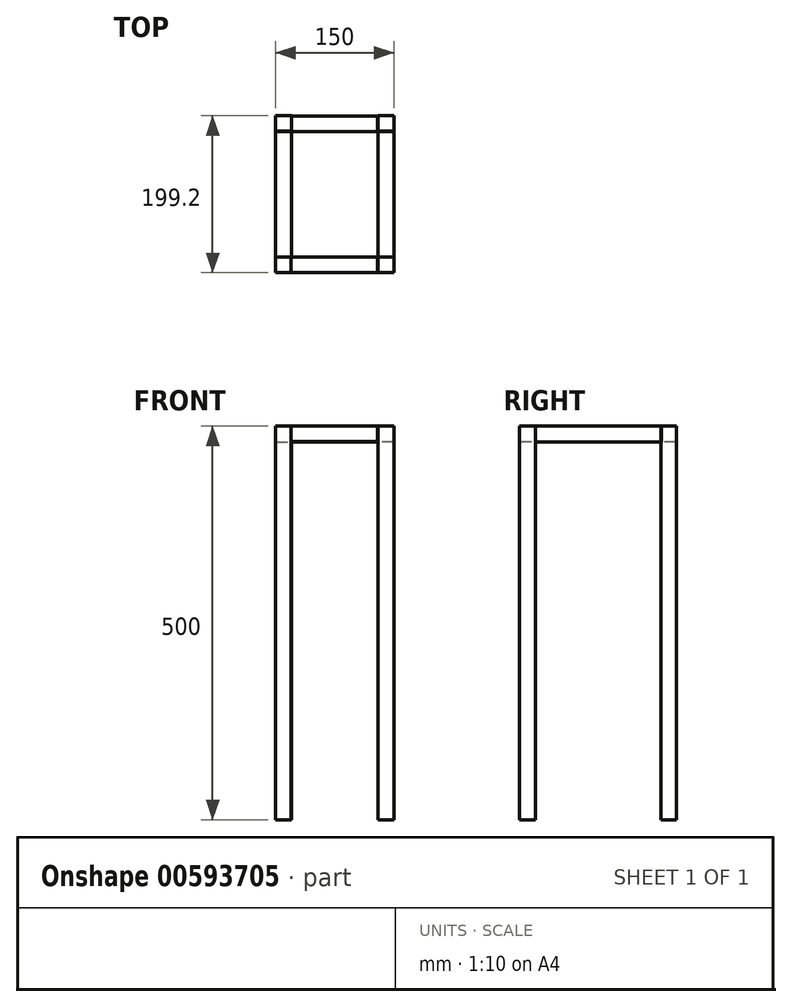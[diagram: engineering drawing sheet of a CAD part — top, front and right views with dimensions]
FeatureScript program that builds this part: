
annotation { "Feature Type Name" : "Feature", "Feature Type Description" : "" }
export const myFeature = defineFeature(function(context is Context, id is Id, definition is map)
    precondition{}
    {
        {
            var Q0;
            Q0=qCreatedBy(makeId("Top.planeOp"),FACE);
            var sketch = newSketch(context, id + "F0", { "sketchPlane" : qUnion([Q0])});
            skLineSegment(sketch, "E0.bottom", {"start": v(0, 0) * mm, "end": v(19.4, 0) * mm});
            skLineSegment(sketch, "E0.top", {"start": v(0, 20) * mm, "end": v(19.4, 20) * mm});
            skLineSegment(sketch, "E0.left", {"start": v(0, 0) * mm, "end": v(0, 20) * mm});
            skLineSegment(sketch, "E0.right", {"start": v(19.4, 0) * mm, "end": v(19.4, 20) * mm});
            skSolve(sketch);
        }
        {
            var Q0;
            Q0=qCreatedBy(makeId("Top.planeOp"),FACE);
            var sketch = newSketch(context, id + "F1", { "sketchPlane" : qUnion([Q0])});
            skLineSegment(sketch, "E1.bottom", {"start": v(0, 0) * mm, "end": v(150, 0) * mm, "construction": true});
            skLineSegment(sketch, "E1.top", {"start": v(0, 199.2) * mm, "end": v(150, 199.2) * mm, "construction": true});
            skLineSegment(sketch, "E1.left", {"start": v(0, 0) * mm, "end": v(0, 199.2) * mm, "construction": true});
            skLineSegment(sketch, "E1.right", {"start": v(150, 0) * mm, "end": v(150, 199.2) * mm, "construction": true});
            skLineSegment(sketch, "E2.bottom", {"start": v(0, 199.2) * mm, "end": v(20, 199.2) * mm});
            skLineSegment(sketch, "E2.top", {"start": v(0, 179.2) * mm, "end": v(20, 179.2) * mm});
            skLineSegment(sketch, "E2.left", {"start": v(0, 199.2) * mm, "end": v(0, 179.2) * mm});
            skLineSegment(sketch, "E2.right", {"start": v(20, 199.2) * mm, "end": v(20, 179.2) * mm});
            skLineSegment(sketch, "E3.bottom", {"start": v(150, 199.2) * mm, "end": v(130, 199.2) * mm});
            skLineSegment(sketch, "E3.top", {"start": v(150, 179.2) * mm, "end": v(130, 179.2) * mm});
            skLineSegment(sketch, "E3.left", {"start": v(150, 199.2) * mm, "end": v(150, 179.2) * mm});
            skLineSegment(sketch, "E3.right", {"start": v(130, 199.2) * mm, "end": v(130, 179.2) * mm});
            skLineSegment(sketch, "E4.bottom", {"start": v(150, 0) * mm, "end": v(130, 0) * mm});
            skLineSegment(sketch, "E4.top", {"start": v(150, 20) * mm, "end": v(130, 20) * mm});
            skLineSegment(sketch, "E4.left", {"start": v(150, 0) * mm, "end": v(150, 20) * mm});
            skLineSegment(sketch, "E4.right", {"start": v(130, 0) * mm, "end": v(130, 20) * mm});
            skLineSegment(sketch, "E5.bottom", {"start": v(0, 0.02) * mm, "end": v(19.4, 0.02) * mm});
            skLineSegment(sketch, "E5.top", {"start": v(0, 20.02) * mm, "end": v(19.4, 20.02) * mm});
            skLineSegment(sketch, "E5.left", {"start": v(0, 0.02) * mm, "end": v(0, 20.02) * mm});
            skLineSegment(sketch, "E5.right", {"start": v(19.4, 0.02) * mm, "end": v(19.4, 20.02) * mm});
            skSolve(sketch);
        }
        {
            var Q0;
            Q0 = qSketchRegion(id + "F1", true);
            extrude(context, id + "F2", {"entities" : qUnion([Q0]), "depth" : 500 * mm, "offsetDistance" : 25 * mm});
        }
        {
            var Q0;
            Q0=makeQuery(id+"F2.opExtrude","SWEPT_FACE",FACE,{"disambiguationData":[OSD([sQuery(id+"F1.wireOp",EDGE,"E4.top")])]});
            var sketch = newSketch(context, id + "F3", { "sketchPlane" : qUnion([Q0])});
            skLineSegment(sketch, "E6.bottom", {"start": v(-150, 500) * mm, "end": v(-130, 500) * mm});
            skLineSegment(sketch, "E6.top", {"start": v(-150, 480) * mm, "end": v(-130, 480) * mm});
            skLineSegment(sketch, "E6.left", {"start": v(-150, 500) * mm, "end": v(-150, 480) * mm});
            skLineSegment(sketch, "E6.right", {"start": v(-130, 500) * mm, "end": v(-130, 480) * mm});
            skLineSegment(sketch, "E7.bottom", {"start": v(0, 500) * mm, "end": v(-20, 500) * mm});
            skLineSegment(sketch, "E7.top", {"start": v(0, 480) * mm, "end": v(-20, 480) * mm});
            skLineSegment(sketch, "E7.left", {"start": v(0, 500) * mm, "end": v(0, 480) * mm});
            skLineSegment(sketch, "E7.right", {"start": v(-20, 500) * mm, "end": v(-20, 480) * mm});
            skSolve(sketch);
        }
        {
            var Q0;
            Q0 = qSketchRegion(id + "F3", true);
            extrude(context, id + "F4", {"entities" : qUnion([Q0]), "depth" : 160 * mm, "offsetDistance" : 25 * mm});
        }
        {
            var Q0;
            Q0=makeQuery(id+"F2.opExtrude","SWEPT_FACE",FACE,{"disambiguationData":[OSD([sQuery(id+"F1.wireOp",EDGE,"E5.right")])]});
            var sketch = newSketch(context, id + "F5", { "sketchPlane" : qUnion([Q0])});
            skLineSegment(sketch, "E8.bottom", {"start": v(0.02, 500) * mm, "end": v(20.02, 500) * mm});
            skLineSegment(sketch, "E8.top", {"start": v(0.02, 480.23) * mm, "end": v(20.02, 480.23) * mm});
            skLineSegment(sketch, "E8.left", {"start": v(0.02, 500) * mm, "end": v(0.02, 480.23) * mm});
            skLineSegment(sketch, "E8.right", {"start": v(20.02, 500) * mm, "end": v(20.02, 480.23) * mm});
            skLineSegment(sketch, "E9.bottom", {"start": v(199.03, 499.96) * mm, "end": v(179.44, 499.96) * mm});
            skLineSegment(sketch, "E9.top", {"start": v(199.03, 479.96) * mm, "end": v(179.44, 479.96) * mm});
            skLineSegment(sketch, "E9.left", {"start": v(199.03, 499.96) * mm, "end": v(199.03, 479.96) * mm});
            skLineSegment(sketch, "E9.right", {"start": v(179.44, 499.96) * mm, "end": v(179.44, 479.96) * mm});
            skSolve(sketch);
        }
        {
            var Q0;
            Q0 = qSketchRegion(id + "F5", true);
            extrude(context, id + "F6", {"entities" : qUnion([Q0]), "depth" : 110 * mm, "offsetDistance" : 25 * mm});
        }
    });
